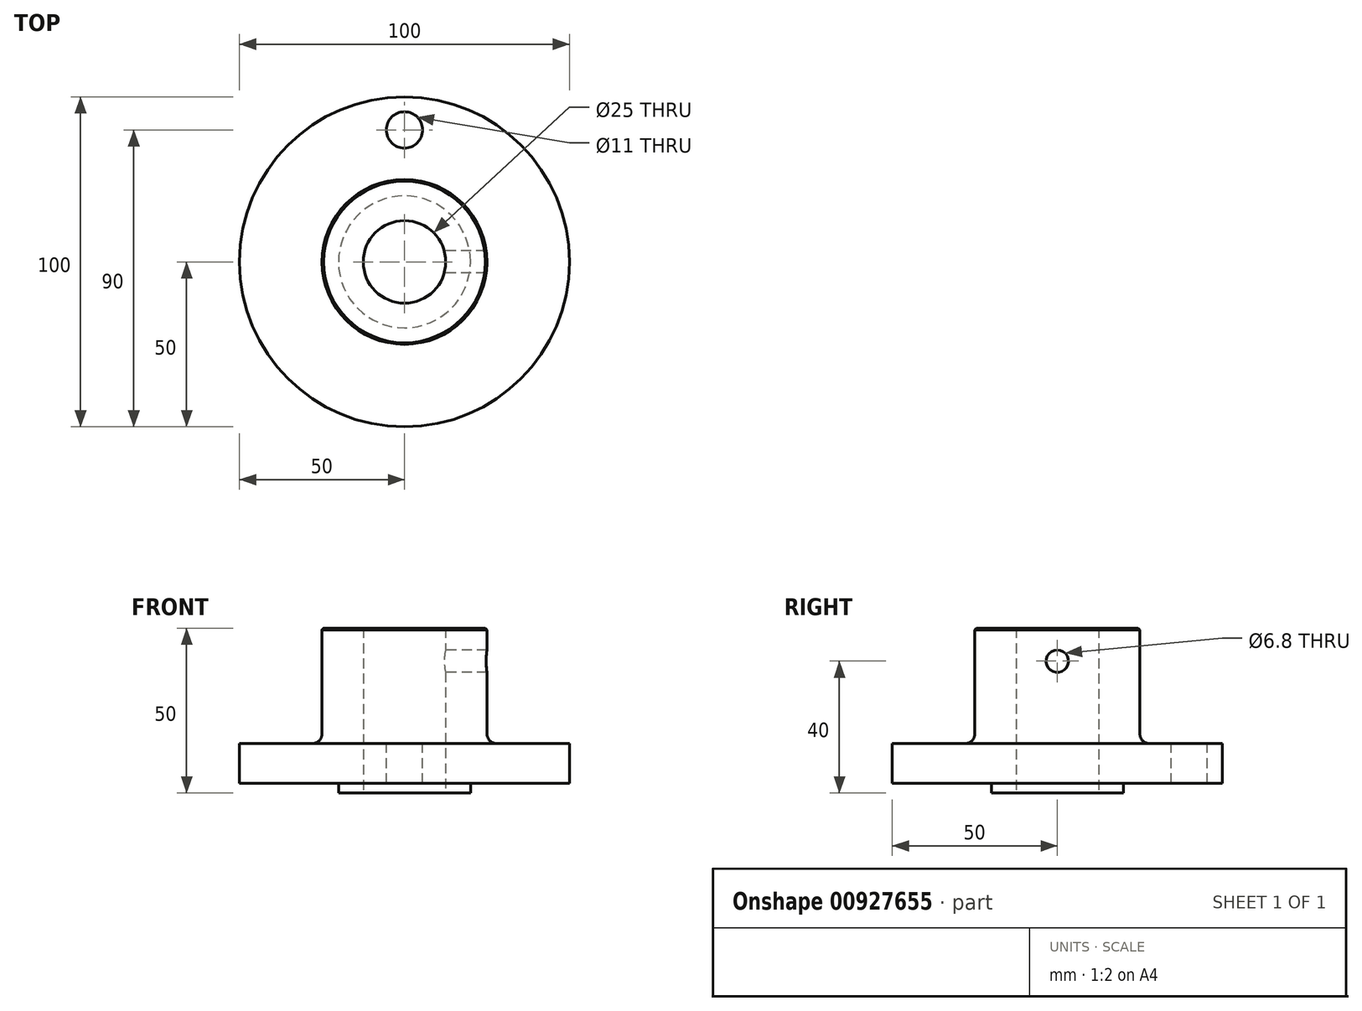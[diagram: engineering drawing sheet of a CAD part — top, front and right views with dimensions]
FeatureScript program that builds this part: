
annotation { "Feature Type Name" : "Feature", "Feature Type Description" : "" }
export const myFeature = defineFeature(function(context is Context, id is Id, definition is map)
    precondition{}
    {
        {
            var Q0;
            Q0=qCreatedBy(makeId("Front.planeOp"),FACE);
            var sketch = newSketch(context, id + "F0", { "sketchPlane" : qUnion([Q0])});
            skLineSegment(sketch, "E0", {"start": v(0, 0) * mm, "end": v(0, 67.45) * mm, "construction": true});
            skLineSegment(sketch, "E1", {"start": v(-12.5, 0) * mm, "end": v(-12.5, 50) * mm});
            skLineSegment(sketch, "E2", {"start": v(-12.5, 50) * mm, "end": v(-25, 50) * mm});
            skLineSegment(sketch, "E3", {"start": v(-25, 50) * mm, "end": v(-25, 15) * mm});
            skLineSegment(sketch, "E4", {"start": v(-25, 15) * mm, "end": v(-50, 15) * mm});
            skLineSegment(sketch, "E5", {"start": v(-50, 15) * mm, "end": v(-50, 3) * mm});
            skLineSegment(sketch, "E6", {"start": v(-50, 3) * mm, "end": v(-20, 3) * mm});
            skLineSegment(sketch, "E7", {"start": v(-20, 3) * mm, "end": v(-20, 0) * mm});
            skLineSegment(sketch, "E8", {"start": v(-20, 0) * mm, "end": v(-12.5, 0) * mm});
            skSolve(sketch);
        }
        {
            var Q0;
            Q0=qSketchRegion(id+"F0",true);
            var Q1;
            Q1=sQuery(id+"F0.wireOp",EDGE,"E0");
            revolve(context, id + "F1", {"surfaceOperationType" : NewSurfaceOperationType.NEW, "entities" : qUnion([Q0]), "axis" : qUnion([Q1]), "revolveType" : RevolveType.FULL});
        }
        {
            var Q0;
            Q0=makeQuery(id+"F1.opRevolve","SWEPT_EDGE",EDGE,{"disambiguationData":[OSD([sQuery(id+"F0.wireOp",EDGE,"E3"),sQuery(id+"F0.wireOp",EDGE,"E4")])]});
            fillet(context, id + "F2", {"entities" : qUnion([Q0]), "radius" : 3 * mm, "tangentPropagation" : true, "allowEdgeOverflow" : false});
        }
        {
            var Q0;
            Q0=qCreatedBy(makeId("Right.planeOp"),FACE);
            var sketch = newSketch(context, id + "F3", { "sketchPlane" : qUnion([Q0])});
            skPoint(sketch, "E9", {"position": v(0, 40) * mm});
            skSolve(sketch);
        }
        {
            var Q0;
            Q0=sQuery(id+"F3.wireOp",VERTEX,"E9");
            var Q1;
            Q1=makeQuery(id+"F1.opRevolve","SWEPT_BODY",BODY,{"disambiguationData":[OSD([sQuery(id+"F0.wireOp",EDGE,"E1"),sQuery(id+"F0.wireOp",EDGE,"E2"),sQuery(id+"F0.wireOp",EDGE,"E3"),sQuery(id+"F0.wireOp",EDGE,"E4"),sQuery(id+"F0.wireOp",EDGE,"E5"),sQuery(id+"F0.wireOp",EDGE,"E6"),sQuery(id+"F0.wireOp",EDGE,"E7"),sQuery(id+"F0.wireOp",EDGE,"E8")])]});
            hole(context, id + "F4", {"style" : HoleStyle.SIMPLE, "endStyle" : HoleEndStyle.THROUGH, "oppositeDirection" : true, "standardTappedOrClearance" : lookupTablePath({ "standard" : "ISO", "engagement" : "75%", "pitch" : "1.25 mm", "size" : "M8", "type" : "Tapped" }), "standardBlindInLast" : lookupTablePath({ "standard" : "ISO", "engagement" : "75%", "pitch" : "1.25 mm", "size" : "M8", "type" : "Tapped" }), "holeDiameter" : 6.8 * mm, "majorDiameter" : 8 * mm, "showTappedDepth" : true, "isTappedThrough" : true, "tappedDepth" : 12 * mm, "tapClearance" : 3, "locations" : qUnion([Q0]), "scope" : qUnion([Q1])});
        }
        {
            var Q0;
            Q0=makeQuery(id+"F1.opRevolve","SWEPT_FACE",FACE,{"disambiguationData":[OSD([sQuery(id+"F0.wireOp",EDGE,"E4")])]});
            var sketch = newSketch(context, id + "F5", { "sketchPlane" : qUnion([Q0])});
            skCircle(sketch, "E10", {"center": v(0, 0) * mm, "radius": 40 * mm, "construction": true});
            skCircle(sketch, "E11", {"center": v(0, 40) * mm, "radius": 5.5 * mm});
            skSolve(sketch);
        }
        {
            var Q0;
            Q0=qSketchRegion(id+"F5",true);
            extrude(context, id + "F6", {"entities" : qUnion([Q0]), "operationType" : NewBodyOperationType.REMOVE, "endBound" : BoundingType.THROUGH_ALL, "oppositeDirection" : true, "depth" : 25 * mm, "offsetDistance" : 25 * mm});
        }
        {
            var Q0;
            Q0=makeQuery(id+"F1.opRevolve","SWEPT_EDGE",EDGE,{"disambiguationData":[OSD([sQuery(id+"F0.wireOp",EDGE,"E2"),sQuery(id+"F0.wireOp",EDGE,"E3")])]});
            chamfer(context, id + "F7", {"entities" : qUnion([Q0]), "width" : 0.5 * mm, "tangentPropagation" : true});
        }
    });
